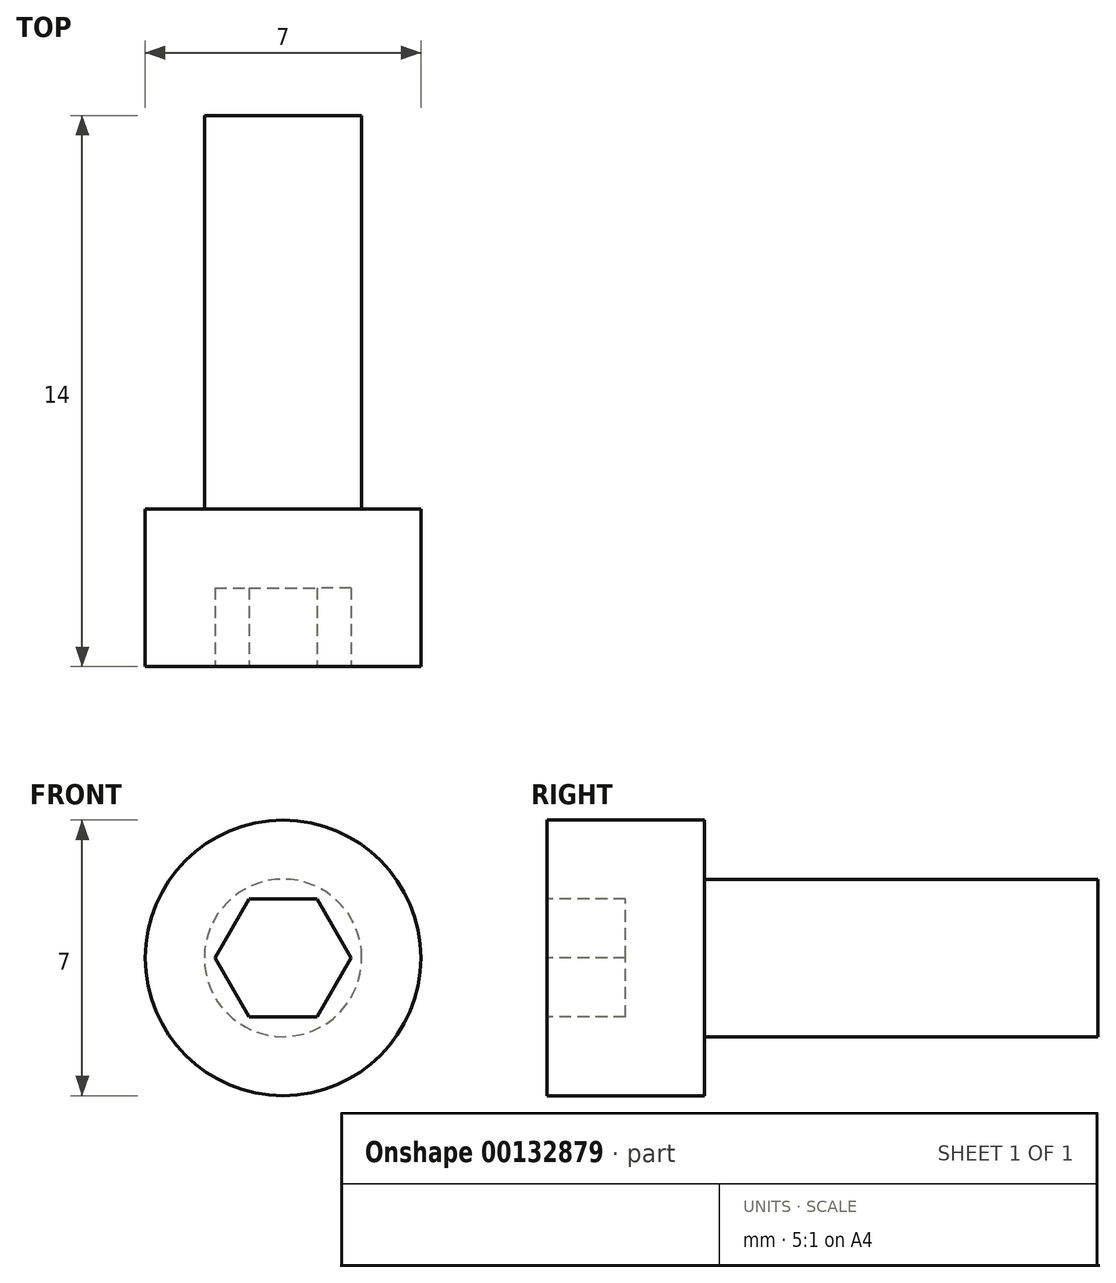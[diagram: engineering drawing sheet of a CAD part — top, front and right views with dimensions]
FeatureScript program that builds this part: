
annotation { "Feature Type Name" : "Feature", "Feature Type Description" : "" }
export const myFeature = defineFeature(function(context is Context, id is Id, definition is map)
    precondition{}
    {
        {
            var Q0;
            Q0=qCreatedBy(makeId("Front.planeOp"),FACE);
            var sketch = newSketch(context, id + "F0", { "sketchPlane" : qUnion([Q0])});
            skCircle(sketch, "E0", {"center": v(0, 0) * mm, "radius": 3.5 * mm});
            skSolve(sketch);
        }
        {
            var Q0;
            Q0 = qSketchRegion(id + "F0", true);
            extrude(context, id + "F1", {"entities" : qUnion([Q0]), "depth" : 4 * mm});
        }
        {
            var Q0;
            Q0=makeQuery(id+"F1.opExtrude","CAP_FACE",FACE,{"disambiguationData":[OSD([sQuery(id+"F0.wireOp",EDGE,"E0")])],"isStart":true});
            var sketch = newSketch(context, id + "F2", { "sketchPlane" : qUnion([Q0])});
            skCircle(sketch, "E1", {"center": v(0, 0) * mm, "radius": 2 * mm});
            skSolve(sketch);
        }
        {
            var Q0;
            Q0 = qSketchRegion(id + "F2", true);
            extrude(context, id + "F3", {"entities" : qUnion([Q0]), "operationType" : NewBodyOperationType.ADD, "depth" : 10 * mm});
        }
        {
            var Q0;
            Q0=makeQuery(id+"F1.opExtrude","CAP_FACE",FACE,{"disambiguationData":[OSD([sQuery(id+"F0.wireOp",EDGE,"E0")])],"isStart":false});
            var sketch = newSketch(context, id + "F4", { "sketchPlane" : qUnion([Q0])});
            skCircle(sketch, "E2.cCircle", {"center": v(0, 0) * mm, "radius": 1.5 * mm, "construction": true});
            skLineSegment(sketch, "E2.0", {"start": v(-0.87, 1.5) * mm, "end": v(0.87, 1.5) * mm});
            skLineSegment(sketch, "E2.1", {"start": v(0.87, 1.5) * mm, "end": v(1.73, 0) * mm});
            skLineSegment(sketch, "E2.2", {"start": v(1.73, 0) * mm, "end": v(0.87, -1.5) * mm});
            skLineSegment(sketch, "E2.3", {"start": v(0.87, -1.5) * mm, "end": v(-0.87, -1.5) * mm});
            skLineSegment(sketch, "E2.4", {"start": v(-0.87, -1.5) * mm, "end": v(-1.73, 0) * mm});
            skLineSegment(sketch, "E2.5", {"start": v(-1.73, 0) * mm, "end": v(-0.87, 1.5) * mm});
            skPoint(sketch, "E2.0.midPoint", {"position": v(0, 1.5) * mm});
            skSolve(sketch);
        }
        {
            var Q0;
            Q0 = qSketchRegion(id + "F4", true);
            extrude(context, id + "F5", {"entities" : qUnion([Q0]), "operationType" : NewBodyOperationType.REMOVE, "oppositeDirection" : true, "depth" : 2 * mm});
        }
    });
